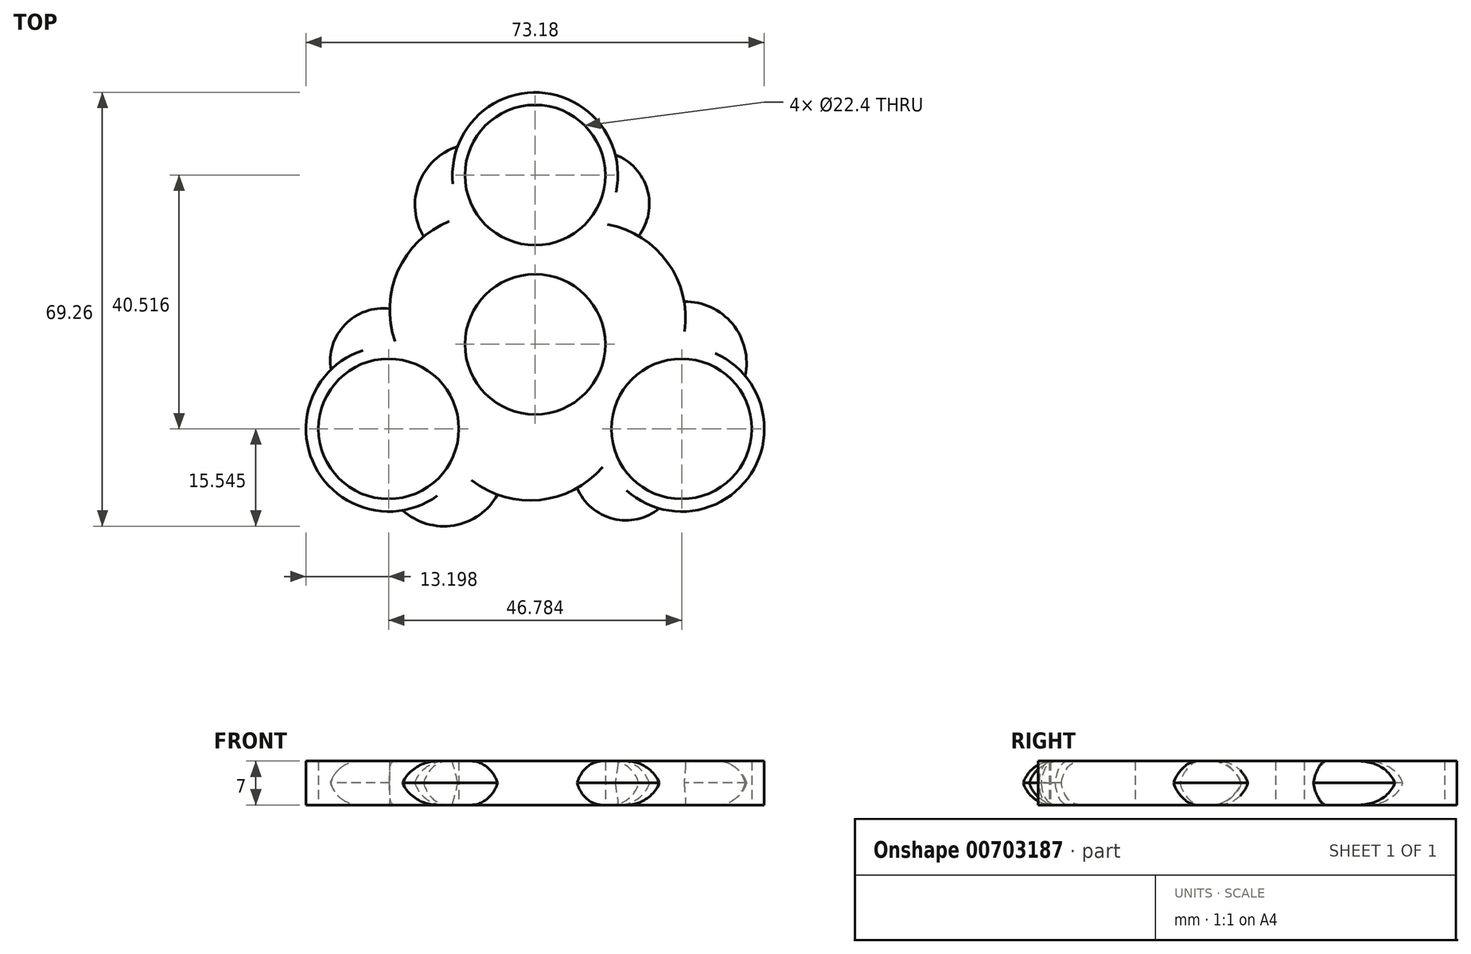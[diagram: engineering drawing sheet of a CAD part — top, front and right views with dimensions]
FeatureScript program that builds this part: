
annotation { "Feature Type Name" : "Feature", "Feature Type Description" : "" }
export const myFeature = defineFeature(function(context is Context, id is Id, definition is map)
    precondition{}
    {
        {
            var Q0;
            Q0=qCreatedBy(makeId("Top.planeOp"),FACE);
            var sketch = newSketch(context, id + "F0", { "sketchPlane" : qUnion([Q0])});
            skCircle(sketch, "E0", {"center": v(0, 0) * mm, "radius": 11.2 * mm});
            skCircle(sketch, "E1", {"center": v(0, 27.01) * mm, "radius": 11.2 * mm});
            skArc(sketch, "E2", {"start": v(10.7, 19.27) * mm, "mid": v(0.66, 40.2) * mm, "end": v(-11.4, 20.37) * mm});
            skArc(sketch, "E3.1.0", {"start": v(-22.04, -0.37) * mm, "mid": v(-35.14, -19.53) * mm, "end": v(-11.94, -20.07) * mm});
            skCircle(sketch, "E3.1.1", {"center": v(-23.4, -13.5) * mm, "radius": 11.2 * mm});
            skArc(sketch, "E3.2.0", {"start": v(11.34, -18.9) * mm, "mid": v(34.48, -20.66) * mm, "end": v(23.35, -0.3) * mm});
            skCircle(sketch, "E3.2.1", {"center": v(23.4, -13.5) * mm, "radius": 11.2 * mm});
            skArc(sketch, "E4", {"start": v(-17.97, 17.04) * mm, "mid": v(-21.77, 12.03) * mm, "end": v(-23.23, 5.9) * mm});
            skArc(sketch, "E5.1.0", {"start": v(-5.78, -24.08) * mm, "mid": v(0.47, -24.87) * mm, "end": v(6.5, -23.07) * mm});
            skArc(sketch, "E5.2.0", {"start": v(23.75, 7.04) * mm, "mid": v(21.3, 12.84) * mm, "end": v(16.73, 17.16) * mm});
            skArc(sketch, "E6", {"start": v(16.73, 17.16) * mm, "mid": v(18.1, 24.87) * mm, "end": v(12.72, 30.55) * mm});
            skArc(sketch, "E7", {"start": v(-12.28, 31.84) * mm, "mid": v(-18.75, 25.84) * mm, "end": v(-17.97, 17.04) * mm});
            skArc(sketch, "E8.1.0", {"start": v(-23.23, 5.9) * mm, "mid": v(-30.58, 3.24) * mm, "end": v(-32.82, -4.26) * mm});
            skArc(sketch, "E8.1.1", {"start": v(-21.43, -26.56) * mm, "mid": v(-13, -29.16) * mm, "end": v(-5.78, -24.08) * mm});
            skArc(sketch, "E8.2.0", {"start": v(6.5, -23.07) * mm, "mid": v(12.49, -28.1) * mm, "end": v(20.1, -26.29) * mm});
            skArc(sketch, "E8.2.1", {"start": v(33.72, -5.28) * mm, "mid": v(31.75, 3.32) * mm, "end": v(23.75, 7.04) * mm});
            skSolve(sketch);
        }
        {
            var Q0;
            Q0=makeQuery(id+"F0.imprint","IMPRINT",FACE,{"disambiguationData":[TD([[makeQuery(id+"F0.imprint","IMPRINT",EDGE,{"derivedFrom":sQuery(id+"F0.wireOp",EDGE,"E0")}),-1.0]])]});
            extrude(context, id + "F1", {"entities" : qUnion([Q0]), "depth" : 7 * mm, "offsetDistance" : 25 * mm});
        }
        {
            var Q0;
            Q0=makeQuery(id+"F1.opExtrude","CAP_EDGE",EDGE,{"disambiguationData":[OSD([sQuery(id+"F0.wireOp",EDGE,"E8.1.0")])],"isStart":true});
            var Q1;
            Q1=makeQuery(id+"F1.opExtrude","CAP_EDGE",EDGE,{"disambiguationData":[OSD([sQuery(id+"F0.wireOp",EDGE,"E8.1.1")])],"isStart":true});
            var Q2;
            Q2=makeQuery(id+"F1.opExtrude","CAP_EDGE",EDGE,{"disambiguationData":[OSD([sQuery(id+"F0.wireOp",EDGE,"E8.2.0")])],"isStart":true});
            var Q3;
            Q3=makeQuery(id+"F1.opExtrude","CAP_EDGE",EDGE,{"disambiguationData":[OSD([sQuery(id+"F0.wireOp",EDGE,"E8.2.1")])],"isStart":true});
            var Q4;
            Q4=makeQuery(id+"F1.opExtrude","CAP_EDGE",EDGE,{"disambiguationData":[OSD([sQuery(id+"F0.wireOp",EDGE,"E6")])],"isStart":true});
            var Q5;
            Q5=makeQuery(id+"F1.opExtrude","CAP_EDGE",EDGE,{"disambiguationData":[OSD([sQuery(id+"F0.wireOp",EDGE,"E7")])],"isStart":true});
            var Q6;
            Q6=makeQuery(id+"F1.opExtrude","CAP_EDGE",EDGE,{"disambiguationData":[OSD([sQuery(id+"F0.wireOp",EDGE,"E8.2.1")])],"isStart":false});
            var Q7;
            Q7=makeQuery(id+"F1.opExtrude","CAP_EDGE",EDGE,{"disambiguationData":[OSD([sQuery(id+"F0.wireOp",EDGE,"E6")])],"isStart":false});
            var Q8;
            Q8=makeQuery(id+"F1.opExtrude","CAP_EDGE",EDGE,{"disambiguationData":[OSD([sQuery(id+"F0.wireOp",EDGE,"E7")])],"isStart":false});
            var Q9;
            Q9=makeQuery(id+"F1.opExtrude","CAP_EDGE",EDGE,{"disambiguationData":[OSD([sQuery(id+"F0.wireOp",EDGE,"E8.1.0")])],"isStart":false});
            var Q10;
            Q10=makeQuery(id+"F1.opExtrude","CAP_EDGE",EDGE,{"disambiguationData":[OSD([sQuery(id+"F0.wireOp",EDGE,"E8.1.1")])],"isStart":false});
            var Q11;
            Q11=makeQuery(id+"F1.opExtrude","CAP_EDGE",EDGE,{"disambiguationData":[OSD([sQuery(id+"F0.wireOp",EDGE,"E8.2.0")])],"isStart":false});
            fillet(context, id + "F2", {"entities" : qUnion([Q0, Q1, Q2, Q3, Q4, Q5, Q6, Q7, Q8, Q9, Q10, Q11]), "radius" : 5 * mm, "tangentPropagation" : true, "allowEdgeOverflow" : false});
        }
    });
